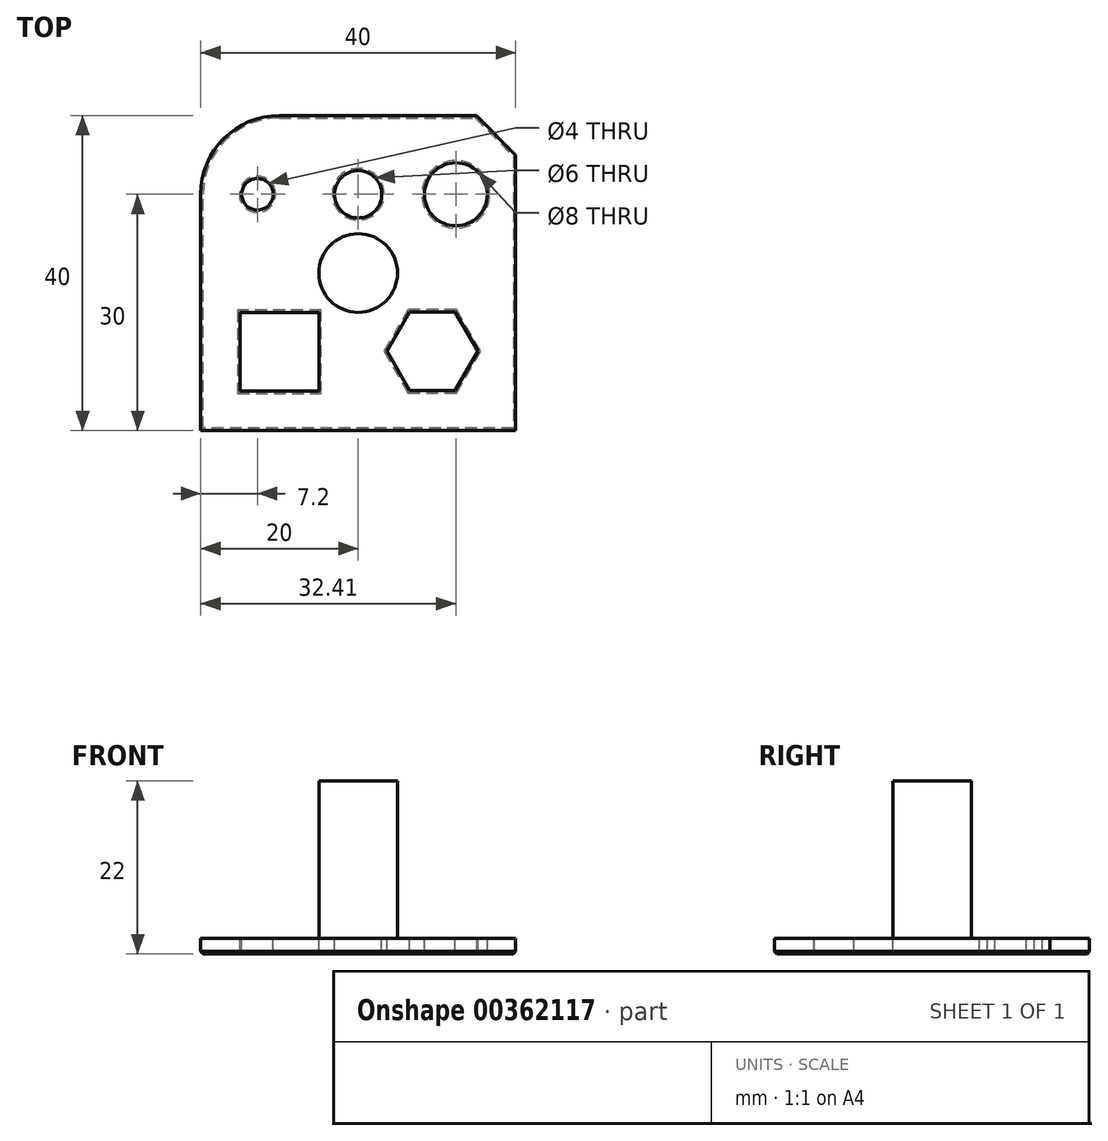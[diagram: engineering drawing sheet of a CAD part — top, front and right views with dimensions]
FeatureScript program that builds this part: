
annotation { "Feature Type Name" : "Feature", "Feature Type Description" : "" }
export const myFeature = defineFeature(function(context is Context, id is Id, definition is map)
    precondition{}
    {
        {
            var Q0;
            Q0=qCreatedBy(makeId("Top.planeOp"),FACE);
            var sketch = newSketch(context, id + "F0", { "sketchPlane" : qUnion([Q0])});
            skLineSegment(sketch, "E0.bottom", {"start": v(-20, 20) * mm, "end": v(20, 20) * mm});
            skLineSegment(sketch, "E0.top", {"start": v(-20, -20) * mm, "end": v(20, -20) * mm});
            skLineSegment(sketch, "E0.left", {"start": v(-20, 20) * mm, "end": v(-20, -20) * mm});
            skLineSegment(sketch, "E0.right", {"start": v(20, 20) * mm, "end": v(20, -20) * mm});
            skPoint(sketch, "E0.middle", {"position": v(0, 0) * mm});
            skSolve(sketch);
        }
        {
            var Q0;
            Q0=makeQuery(id+"F0.imprint","IMPRINT",FACE,{"disambiguationData":[TD([[makeQuery(id+"F0.imprint","IMPRINT",EDGE,{"derivedFrom":sQuery(id+"F0.wireOp",EDGE,"E0.bottom")}),-1.0]])]});
            extrude(context, id + "F1", {"entities" : qUnion([Q0]), "depth" : 2 * mm, "offsetDistance" : 25 * mm});
        }
        {
            var Q0;
            Q0=makeQuery(id+"F1.opExtrude","CAP_FACE",FACE,{"disambiguationData":[OSD([sQuery(id+"F0.wireOp",EDGE,"E0.bottom"),sQuery(id+"F0.wireOp",EDGE,"E0.top"),sQuery(id+"F0.wireOp",EDGE,"E0.left"),sQuery(id+"F0.wireOp",EDGE,"E0.right")])],"isStart":false});
            var sketch = newSketch(context, id + "F2", { "sketchPlane" : qUnion([Q0])});
            skLineSegment(sketch, "E1", {"start": v(-20, 10) * mm, "end": v(20, 10) * mm, "construction": true});
            skCircle(sketch, "E2", {"center": v(-12.8, 10) * mm, "radius": 2 * mm});
            skCircle(sketch, "E3", {"center": v(0, 10) * mm, "radius": 3 * mm});
            skCircle(sketch, "E4", {"center": v(12.41, 10) * mm, "radius": 4 * mm});
            skLineSegment(sketch, "E5.bottom", {"start": v(-15, -5) * mm, "end": v(-5, -5) * mm});
            skLineSegment(sketch, "E5.top", {"start": v(-15, -15) * mm, "end": v(-5, -15) * mm});
            skLineSegment(sketch, "E5.left", {"start": v(-15, -5) * mm, "end": v(-15, -15) * mm});
            skLineSegment(sketch, "E5.right", {"start": v(-5, -5) * mm, "end": v(-5, -15) * mm});
            skPoint(sketch, "E5.middle", {"position": v(-10, -10) * mm});
            skCircle(sketch, "E6.cCircle", {"center": v(9.42, -9.94) * mm, "radius": 5 * mm, "construction": true});
            skLineSegment(sketch, "E6.0", {"start": v(6.53, -4.94) * mm, "end": v(12.3, -4.94) * mm});
            skLineSegment(sketch, "E6.1", {"start": v(12.3, -4.94) * mm, "end": v(15.2, -9.94) * mm});
            skLineSegment(sketch, "E6.2", {"start": v(15.2, -9.94) * mm, "end": v(12.3, -14.94) * mm});
            skLineSegment(sketch, "E6.3", {"start": v(12.3, -14.94) * mm, "end": v(6.53, -14.94) * mm});
            skLineSegment(sketch, "E6.4", {"start": v(6.53, -14.94) * mm, "end": v(3.65, -9.94) * mm});
            skLineSegment(sketch, "E6.5", {"start": v(3.65, -9.94) * mm, "end": v(6.53, -4.94) * mm});
            skPoint(sketch, "E6.0.midPoint", {"position": v(9.42, -4.94) * mm});
            skSolve(sketch);
        }
        {
            var Q0;
            Q0 = qSketchRegion(id + "F2", true);
            var Q1;
            Q1=makeQuery(id+"F1.opExtrude","CAP_FACE",FACE,{"disambiguationData":[OSD([sQuery(id+"F0.wireOp",EDGE,"E0.bottom"),sQuery(id+"F0.wireOp",EDGE,"E0.top"),sQuery(id+"F0.wireOp",EDGE,"E0.left"),sQuery(id+"F0.wireOp",EDGE,"E0.right")])],"isStart":true});
            extrude(context, id + "F3", {"entities" : qUnion([Q0]), "operationType" : NewBodyOperationType.REMOVE, "endBound" : BoundingType.UP_TO_SURFACE, "oppositeDirection" : true, "depth" : 25 * mm, "endBoundEntityFace" : qUnion([Q1]), "offsetDistance" : 25 * mm});
        }
        {
            var Q0;
            Q0=makeQuery(id+"F1.opExtrude","SWEPT_EDGE",EDGE,{"disambiguationData":[OSD([sQuery(id+"F0.wireOp",EDGE,"E0.bottom"),sQuery(id+"F0.wireOp",EDGE,"E0.left")])]});
            fillet(context, id + "F4", {"entities" : qUnion([Q0]), "radius" : 10 * mm, "tangentPropagation" : true, "allowEdgeOverflow" : false});
        }
        {
            var Q0;
            Q0=makeQuery(id+"F1.opExtrude","SWEPT_EDGE",EDGE,{"disambiguationData":[OSD([sQuery(id+"F0.wireOp",EDGE,"E0.bottom"),sQuery(id+"F0.wireOp",EDGE,"E0.right")])]});
            chamfer(context, id + "F5", {"entities" : qUnion([Q0]), "width" : 5 * mm, "tangentPropagation" : true});
        }
        {
            var Q0;
            Q0=makeQuery(id+"F1.opExtrude","CAP_FACE",FACE,{"disambiguationData":[OSD([sQuery(id+"F0.wireOp",EDGE,"E0.bottom"),sQuery(id+"F0.wireOp",EDGE,"E0.top"),sQuery(id+"F0.wireOp",EDGE,"E0.left"),sQuery(id+"F0.wireOp",EDGE,"E0.right")])],"isStart":false});
            var sketch = newSketch(context, id + "F6", { "sketchPlane" : qUnion([Q0])});
            skCircle(sketch, "E7", {"center": v(0, 0) * mm, "radius": 5 * mm});
            skSolve(sketch);
        }
        {
            var Q0;
            Q0=makeQuery(id+"F6.imprint","IMPRINT",FACE,{"disambiguationData":[TD([[makeQuery(id+"F6.imprint","IMPRINT",EDGE,{"derivedFrom":sQuery(id+"F6.wireOp",EDGE,"E7")}),1.0]])]});
            extrude(context, id + "F7", {"entities" : qUnion([Q0]), "operationType" : NewBodyOperationType.ADD, "depth" : 20 * mm, "offsetDistance" : 25 * mm});
        }
        {
            var Q0;
            Q0=makeQuery(id+"F1.opExtrude","CAP_FACE",FACE,{"disambiguationData":[OSD([sQuery(id+"F0.wireOp",EDGE,"E0.bottom"),sQuery(id+"F0.wireOp",EDGE,"E0.top"),sQuery(id+"F0.wireOp",EDGE,"E0.left"),sQuery(id+"F0.wireOp",EDGE,"E0.right")])],"isStart":true});
            chamfer(context, id + "F8", {"entities" : qUnion([Q0]), "width" : 0.3 * mm, "tangentPropagation" : true});
        }
    });
